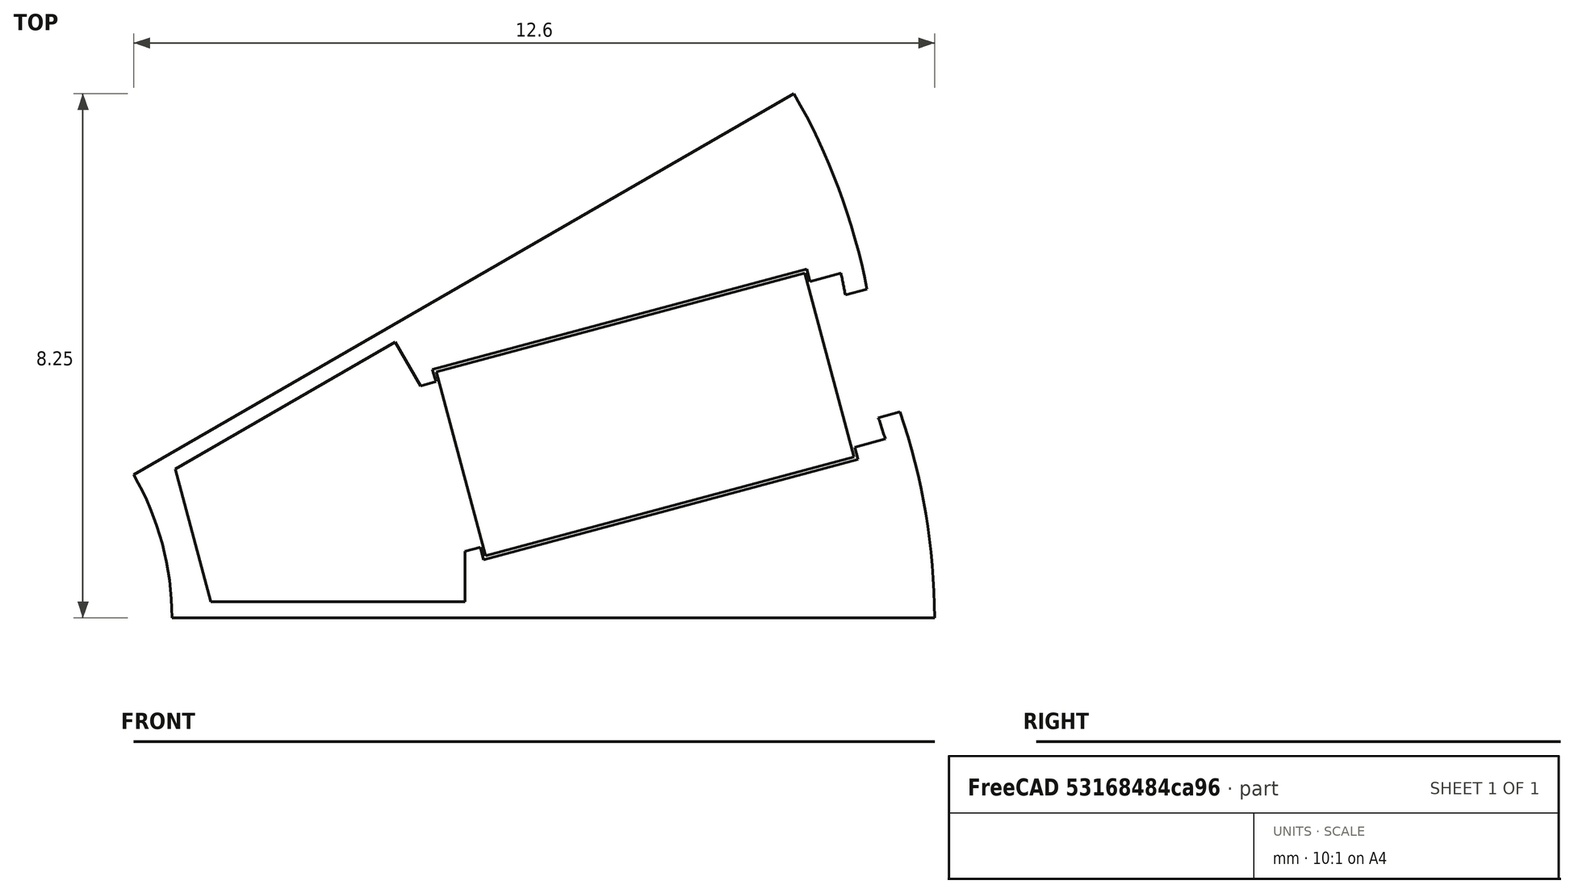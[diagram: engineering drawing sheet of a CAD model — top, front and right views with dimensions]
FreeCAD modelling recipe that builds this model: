
FCSTD DOCUMENT  (FreeCAD 0.18R4 (GitTag))
Label: rotor2
License: All rights reserved
LicenseURL: http://en.wikipedia.org/wiki/All_rights_reserved
objects: Sketcher::SketchObject×6, Surface::Filling×3, PartDesign::Body×2, Spreadsheet::Sheet×1, Part::Cut×1
note: 12 computed .brp shape members not serialized (recipe doc carries the construction recipe); baked Part::Feature solids carry a one-line shape summary decoded from their .brp

FEATURE [Spreadsheet::Sheet] Spreadsheet  label="Variables"
  cells = A1=poleNumber; B1(poleNumber)=12; A2=outerDiameter; B2(outerDiameter)=33; A3=innerDiameter; B3(innerDiameter)=9; D3=Calc Value; A4=stackLength; B4(stackLength)=20; D4=Input Value; A5=stackingFactor; B5(stackingFactor)=0.95; A6=embrace; B6(embrace)=75; A7=contourRatio; B7(contourRatio)=60; A8=magnetAirgap; B8(magnetAirgap)=0.05; A9=poleSeparation; B9(poleSeparation)=2; A10=magnetWidth; B10(magnetWidth)=3; A11=magnetHeight; B11(magnetHeight)=6; A12=rib; B12(rib)=0.5; A13=bridgeCurved; B13(bridgeCurved)=0.35; A14=cutTop; B14(cutTop)=0.2; A15=cutBottom; B15(cutBottom)=0.25; A16=segmentAngle; B16(segmentAngle)==360 / poleNumber; A17=movePocketInwards; B17(movePocketInwards)=0.5; A18=cuttingThickness; B18(cuttingThickness)=0.1; A19=magnetLength; B19(magnetLength)==stackLength; A20=cut; B20(cut)=0.2; A21=ribShaft; B21(ribShaft)=0.5; A22=magnetEmbrace; B22(magnetEmbrace)=70; A23=magnetContourRatio; B23(magnetContourRatio)=95; A24=axialMisalignment; B24(axialMisalignment)=0.5
FEATURE [Sketcher::SketchObject] Sketch003  label="RotorPoleSketch"
  MapMode = 5
  Support = -> [XY_Plane]
  expr: Constraints[21] = Variables.innerDiameter / 2
  expr: Constraints[27] = Variables.segmentAngle / 2
  expr: Constraints[9] = Variables.outerDiameter / 2 * Variables.contourRatio / 100
  expr: Constraints[14] = Variables.poleSeparation
  expr: Constraints[11] = Variables.outerDiameter / 2 * Variables.contourRatio / 100
  expr: Constraints[6] = Variables.outerDiameter / 2
  expr: Constraints[5] = Variables.segmentAngle
  sketch-geometry (10):
    g0: LineSegment [constr] StartX=0 StartY=-1e-16 StartZ=0 EndX=16.5 EndY=-1e-16 EndZ=0
    g1: LineSegment [constr] StartX=0 StartY=-1e-16 StartZ=0 EndX=14.2894 EndY=8.25 EndZ=0
    g2: ArcOfCircle [constr] CenterX=0 CenterY=-1e-16 CenterZ=0 NormalX=0 NormalY=0 NormalZ=1 AngleXU=0 Radius=16.5 StartAngle=0 EndAngle=0.523599
    g3: ArcOfCircle CenterX=5.71577 CenterY=3.3 CenterZ=0 NormalX=0 NormalY=0 NormalZ=1 AngleXU=0 Radius=9.9 StartAngle=0.190202 EndAngle=0.523599
    g4: ArcOfCircle CenterX=6.6 CenterY=-5.416e-11 CenterZ=0 NormalX=0 NormalY=0 NormalZ=1 AngleXU=0 Radius=9.9 StartAngle=5.4707e-12 EndAngle=0.333396
    g5: LineSegment StartX=15.4372 StartY=5.17167 StartZ=0 EndX=15.9549 EndY=3.23982 EndZ=0
    g6: LineSegment [constr] StartX=0 StartY=0 StartZ=0 EndX=15.9378 EndY=4.27051 EndZ=0
    g7: ArcOfCircle CenterX=0 CenterY=0 CenterZ=0 NormalX=0 NormalY=0 NormalZ=1 AngleXU=0 Radius=4.5 StartAngle=0 EndAngle=0.523599
    g8: LineSegment StartX=3.89711 StartY=2.25 StartZ=0 EndX=14.2894 EndY=8.25 EndZ=0
    g9: LineSegment StartX=4.5 StartY=0 StartZ=0 EndX=16.5 EndY=-1e-16 EndZ=0
  constraints (28):
    c: Coincident(g0,g-1)
    c: Coincident(g1,g0)
    c: Coincident(g2,g0)
    c: Coincident(g2,g0)
    c: Coincident(g2,g1)
    c: Angle(g0,g1) = 0.523599
    c: Radius(g2) = 16.5
    c: PointOnObject(g3,g1)
    c: Coincident(g3,g1)
    c: Radius(g3) = 9.9
    c: Coincident(g4,g0)
    c: Radius(g4) = 9.9
    c: Coincident(g5,g3)
    c: Coincident(g5,g4)
    c: Distance(g5) = 2
    c: Coincident(g6,g-1)
    c: PointOnObject(g6,g2)
    c: Symmetric(g3,g4,g6)
    c: Coincident(g7,g-1)
    c: PointOnObject(g7,g1)
    c: PointOnObject(g7,g0)
    c: Radius(g7) = 4.5
    c: Coincident(g8,g7)
    c: Coincident(g8,g3)
    c: Coincident(g9,g7)
    c: Coincident(g9,g4)
    c: Horizontal(g0)
    c: Angle(g-1,g6) = 0.261799
FEATURE [Sketcher::SketchObject] Sketch004  label="BoundingBox"
  MapMode = 5
  Support = -> [XY_Plane]
  expr: Constraints[8] = Variables.outerDiameter
  sketch-geometry (6):
    g0: LineSegment StartX=-16.5 StartY=-16.5 StartZ=0 EndX=16.5 EndY=-16.5 EndZ=0
    g1: LineSegment StartX=16.5 StartY=-16.5 StartZ=0 EndX=16.5 EndY=16.5 EndZ=0
    g2: LineSegment StartX=16.5 StartY=16.5 StartZ=0 EndX=-16.5 EndY=16.5 EndZ=0
    g3: LineSegment StartX=-16.5 StartY=16.5 StartZ=0 EndX=-16.5 EndY=-16.5 EndZ=0
    g4: LineSegment [constr] StartX=-16.5 StartY=-16.5 StartZ=0 EndX=16.5 EndY=16.5 EndZ=0
    g5: GeomPoint X=0 Y=0 Z=0
  constraints (14):
    c: Coincident(g0,g1)
    c: Coincident(g1,g2)
    c: Coincident(g2,g3)
    c: Coincident(g3,g0)
    c: Horizontal(g0)
    c: Horizontal(g2)
    c: Vertical(g1)
    c: Vertical(g3)
    c: DistanceY(g1,g1) = 33
    c: Equal(g2,g1)
    c: Coincident(g4,g0)
    c: Coincident(g4,g1)
    c: Symmetric(g0,g1,g5)
    c: Coincident(g-1,g5)
FEATURE [Sketcher::SketchObject] Sketch005  label="RotorSideSketch"
  MapMode = 5
  Support = -> [XY_Plane001]
  expr: Constraints[22] = Variables.stackLength / 2 - Variables.axialMisalignment
  expr: Constraints[9] = Variables.outerDiameter / 2
  expr: Constraints[8] = Variables.innerDiameter / 2
  expr: Constraints[7] = Variables.stackLength
  sketch-geometry (8):
    g0: LineSegment StartX=-9.5 StartY=4.5 StartZ=0 EndX=10.5 EndY=4.5 EndZ=0
    g1: LineSegment StartX=10.5 StartY=4.5 StartZ=0 EndX=10.5 EndY=16.5 EndZ=0
    g2: LineSegment StartX=10.5 StartY=16.5 StartZ=0 EndX=-9.5 EndY=16.5 EndZ=0
    g3: LineSegment StartX=-9.5 StartY=16.5 StartZ=0 EndX=-9.5 EndY=4.5 EndZ=0
    g4: LineSegment StartX=-9.5 StartY=-4.5 StartZ=0 EndX=10.5 EndY=-4.5 EndZ=0
    g5: LineSegment StartX=10.5 StartY=-4.5 StartZ=0 EndX=10.5 EndY=-16.5 EndZ=0
    g6: LineSegment StartX=10.5 StartY=-16.5 StartZ=0 EndX=-9.5 EndY=-16.5 EndZ=0
    g7: LineSegment StartX=-9.5 StartY=-16.5 StartZ=0 EndX=-9.5 EndY=-4.5 EndZ=0
  constraints (23):
    c: Coincident(g0,g1)
    c: Coincident(g1,g2)
    c: Coincident(g2,g3)
    c: Coincident(g3,g0)
    c: Horizontal(g0)
    c: Vertical(g1)
    c: Vertical(g3)
    c: DistanceX(g2,g2) = 20
    c: DistanceY(g-1,g0) = 4.5
    c: DistanceY(g-1,g1) = 16.5
    c: Coincident(g4,g5)
    c: Coincident(g5,g6)
    c: Coincident(g6,g7)
    c: Coincident(g7,g4)
    c: Horizontal(g4)
    c: Vertical(g5)
    c: Vertical(g7)
    c: Equal(g4,g0)
    c: Equal(g7,g3)
    c: Horizontal(g2)
    c: Horizontal(g6)
    c: Symmetric(g4,g0,g-1)
    c: DistanceX(g0,g-1) = 9.5
FEATURE [Sketcher::SketchObject] Sketch006  label="MagnetSideSketch"
  ExternalGeometry = -> [Sketch005]
  MapMode = 5
  Support = -> [XY_Plane001]
  expr: Constraints[23] = Variables.stackLength / 2 - Variables.axialMisalignment
  expr: Constraints[12] = Variables.bridgeCurved + Variables.movePocketInwards
  expr: Constraints[8] = Variables.magnetHeight
  expr: Constraints[7] = Variables.magnetLength
  sketch-geometry (9):
    g0: LineSegment StartX=-9.5 StartY=9.65 StartZ=0 EndX=10.5 EndY=9.65 EndZ=0
    g1: LineSegment StartX=10.5 StartY=9.65 StartZ=0 EndX=10.5 EndY=15.65 EndZ=0
    g2: LineSegment StartX=10.5 StartY=15.65 StartZ=0 EndX=-9.5 EndY=15.65 EndZ=0
    g3: LineSegment StartX=-9.5 StartY=15.65 StartZ=0 EndX=-9.5 EndY=9.65 EndZ=0
    g4: LineSegment [constr] StartX=10.5 StartY=15.65 StartZ=0 EndX=10.5 EndY=16.5 EndZ=0
    g5: LineSegment StartX=-9.5 StartY=-15.65 StartZ=0 EndX=10.5 EndY=-15.65 EndZ=0
    g6: LineSegment StartX=10.5 StartY=-15.65 StartZ=0 EndX=10.5 EndY=-9.65 EndZ=0
    g7: LineSegment StartX=10.5 StartY=-9.65 StartZ=0 EndX=-9.5 EndY=-9.65 EndZ=0
    g8: LineSegment StartX=-9.5 StartY=-9.65 StartZ=0 EndX=-9.5 EndY=-15.65 EndZ=0
  constraints (25):
    c: Coincident(g0,g1)
    c: Coincident(g1,g2)
    c: Coincident(g2,g3)
    c: Coincident(g3,g0)
    c: Horizontal(g0)
    c: Vertical(g1)
    c: Vertical(g3)
    c: DistanceX(g2,g2) = 20
    c: DistanceY(g1,g1) = 6
    c: Coincident(g4,g1)
    c: PointOnObject(g4,g-3)
    c: Angle(g4,g2) = 1.5708
    c: DistanceY(g4,g4) = 0.85
    c: Coincident(g5,g6)
    c: Coincident(g6,g7)
    c: Coincident(g7,g8)
    c: Coincident(g8,g5)
    c: Horizontal(g5)
    c: Vertical(g6)
    c: Vertical(g8)
    c: Symmetric(g7,g0,g-1)
    c: Symmetric(g6,g0,g-1)
    c: Equal(g8,g3)
    c: DistanceX(g0,g-1) = 9.5
    c: Horizontal(g2)
FEATURE [PartDesign::Body] Body001  label="SideView"
  Group = -> [Sketch005,Sketch006]
  Origin = -> Origin001
FEATURE [Surface::Filling] Surface001  label="RotorPoleSketch_Surface"
  Anisotropy = false
  BoundaryEdges = -> [Sketch003]
  BoundaryOrder = [0,0,0,0,0,0]
  Degree = 3
  Iterations = 2
  MaximumDegree = 8
  MaximumSegments = 9
  PointsOnCurve = 15
  TolAngular = 0.01
  TolCurvature = 0.1
  Tolerance2d = 1e-05
  Tolerance3d = 0.0001
FEATURE [Sketcher::SketchObject] Sketch008  label="PocketSketch"
  MapMode = 5
  Support = -> [XY_Plane]
  expr: Constraints[89] = Variables.innerDiameter / 2 + Variables.ribShaft
  expr: Constraints[48] = Variables.magnetWidth + 2 * Variables.magnetAirgap
  expr: Constraints[36] = Variables.magnetWidth + 2 * Variables.magnetAirgap - 2 * Variables.cut
  expr: Constraints[66] = Variables.rib / 2
  expr: Constraints[25] = Variables.outerDiameter / 2 * Variables.contourRatio / 100 - Variables.bridgeCurved
  expr: Constraints[21] = Variables.segmentAngle / 2
  expr: Constraints[55] = Variables.magnetHeight + 2 * Variables.magnetAirgap
  expr: Constraints[41] = Variables.movePocketInwards
  expr: Constraints[9] = Variables.outerDiameter / 2 * Variables.contourRatio / 100
  expr: Constraints[14] = Variables.poleSeparation
  expr: Constraints[23] = Variables.outerDiameter / 2 * Variables.contourRatio / 100 - Variables.bridgeCurved
  expr: Constraints[19] = Variables.innerDiameter / 2
  expr: Constraints[11] = Variables.outerDiameter / 2 * Variables.contourRatio / 100
  expr: Constraints[6] = Variables.outerDiameter / 2
  expr: Constraints[72] = Variables.rib / 2
  expr: Constraints[5] = Variables.segmentAngle
  sketch-geometry (31):
    g0: LineSegment [constr] StartX=0 StartY=-5e-16 StartZ=0 EndX=16.5 EndY=-5e-16 EndZ=0
    g1: LineSegment [constr] StartX=0 StartY=-5e-16 StartZ=0 EndX=14.2894 EndY=8.25 EndZ=0
    g2: ArcOfCircle [constr] CenterX=0 CenterY=-5e-16 CenterZ=0 NormalX=0 NormalY=0 NormalZ=1 AngleXU=0 Radius=16.5 StartAngle=0 EndAngle=0.523599
    g3: ArcOfCircle [constr] CenterX=5.71577 CenterY=3.3 CenterZ=0 NormalX=0 NormalY=0 NormalZ=1 AngleXU=0 Radius=9.9 StartAngle=0.190202 EndAngle=0.523599
    g4: ArcOfCircle [constr] CenterX=6.6 CenterY=-3.5e-15 CenterZ=0 NormalX=0 NormalY=0 NormalZ=1 AngleXU=0 Radius=9.9 StartAngle=3e-16 EndAngle=0.333396
    g5: LineSegment StartX=15.4372 StartY=5.17167 StartZ=0 EndX=15.9549 EndY=3.23982 EndZ=0
    g6: LineSegment [constr] StartX=0 StartY=0 StartZ=0 EndX=15.6961 EndY=4.20574 EndZ=0
    g7: ArcOfCircle [constr] CenterX=0 CenterY=0 CenterZ=0 NormalX=0 NormalY=0 NormalZ=1 AngleXU=0 Radius=4.5 StartAngle=0 EndAngle=0.523599
    g8: ArcOfCircle CenterX=5.71577 CenterY=3.3 CenterZ=0 NormalX=0 NormalY=0 NormalZ=1 AngleXU=0 Radius=9.55 StartAngle=0.187574 EndAngle=0.224282
    g9: ArcOfCircle CenterX=6.6 CenterY=-3.5e-15 CenterZ=0 NormalX=0 NormalY=0 NormalZ=1 AngleXU=0 Radius=9.55 StartAngle=0.299317 EndAngle=0.336025
    g10: LineSegment StartX=15.0983 StartY=5.08084 StartZ=0 EndX=15.4372 EndY=5.17167 EndZ=0
    g11: LineSegment StartX=15.6159 StartY=3.14899 StartZ=0 EndX=15.9549 EndY=3.23982 EndZ=0
    g12: LineSegment [constr] StartX=15.0266 StartY=5.42398 StartZ=0 EndX=15.7254 EndY=2.81598 EndZ=0
    g13: LineSegment StartX=15.0266 StartY=5.42398 StartZ=0 EndX=14.5436 EndY=5.29457 EndZ=0
    g14: LineSegment StartX=15.7254 StartY=2.81598 StartZ=0 EndX=15.2424 EndY=2.68657 EndZ=0
    g15: LineSegment StartX=14.5436 StartY=5.29457 StartZ=0 EndX=14.4919 EndY=5.48776 EndZ=0
    g16: LineSegment StartX=15.2424 StartY=2.68657 StartZ=0 EndX=15.2942 EndY=2.49339 EndZ=0
    g17: LineSegment StartX=14.4919 StartY=5.48776 StartZ=0 EndX=8.5997 EndY=3.90896 EndZ=0
    g18: LineSegment StartX=15.2942 StartY=2.49339 StartZ=0 EndX=9.40204 EndY=0.914592 EndZ=0
    g19: LineSegment StartX=8.5997 StartY=3.90896 StartZ=0 EndX=8.65147 EndY=3.71578 EndZ=0
    g20: LineSegment StartX=9.40204 StartY=0.914592 StartZ=0 EndX=9.35028 EndY=1.10778 EndZ=0
    g21: LineSegment StartX=8.65147 StartY=3.71578 StartZ=0 EndX=8.40999 EndY=3.65107 EndZ=0
    g22: LineSegment StartX=9.35028 StartY=1.10778 StartZ=0 EndX=9.1088 EndY=1.04307 EndZ=0
    g23: LineSegment StartX=8.40999 StartY=3.65107 StartZ=0 EndX=8.01345 EndY=4.33789 EndZ=0
    g24: LineSegment [constr] StartX=8.01345 StartY=4.33789 StartZ=0 EndX=7.88845 EndY=4.5544 EndZ=0
    g25: LineSegment StartX=9.1088 StartY=1.04307 StartZ=0 EndX=9.1088 EndY=0.25 EndZ=0
    g26: LineSegment [constr] StartX=9.1088 StartY=0.25 StartZ=0 EndX=9.1088 EndY=0 EndZ=0
    g27: LineSegment StartX=8.01345 StartY=4.33789 StartZ=0 EndX=4.54986 EndY=2.33819 EndZ=0
    g28: LineSegment StartX=4.54986 StartY=2.33819 StartZ=0 EndX=5.10939 EndY=0.25 EndZ=0
    g29: LineSegment StartX=5.10939 StartY=0.25 StartZ=0 EndX=9.1088 EndY=0.25 EndZ=0
    g30: LineSegment [constr] StartX=0 StartY=0 StartZ=0 EndX=4.82963 EndY=1.2941 EndZ=0
  constraints (91):
    c: Coincident(g0,g-1)
    c: Coincident(g1,g0)
    c: Coincident(g2,g0)
    c: Coincident(g2,g0)
    c: Coincident(g2,g1)
    c: Angle(g0,g1) = 0.523599
    c: Radius(g2) = 16.5
    c: PointOnObject(g3,g1)
    c: Coincident(g3,g1)
    c: Radius(g3) = 9.9
    c: Coincident(g4,g0)
    c: Radius(g4) = 9.9
    c: Coincident(g5,g3)
    c: Coincident(g5,g4)
    c: Distance(g5) = 2
    c: Coincident(g6,g-1)
    c: Coincident(g7,g-1)
    c: PointOnObject(g7,g1)
    c: PointOnObject(g7,g0)
    c: Radius(g7) = 4.5
    c: Horizontal(g0)
    c: Angle(g-1,g6) = 0.261799
    c: Coincident(g8,g3)
    c: Radius(g8) = 9.55
    c: Coincident(g9,g4)
    c: Radius(g9) = 9.55
    c: Coincident(g10,g8)
    c: Coincident(g10,g3)
    c: Coincident(g11,g9)
    c: Coincident(g11,g4)
    c: Parallel(g11,g6)
    c: Parallel(g10,g6)
    c: Symmetric(g11,g10,g6)
    c: PointOnObject(g6,g5)
    c: Coincident(g12,g8)
    c: Coincident(g12,g9)
    c: Distance(g12) = 2.7
    c: Perpendicular(g6,g12)
    c: Coincident(g13,g8)
    c: Coincident(g14,g9)
    c: Equal(g14,g13)
    c: Distance(g13) = 0.5
    c: Angle(g13,g12) = 1.5708
    c: Angle(g12,g14) = 1.5708
    c: Coincident(g15,g13)
    c: Coincident(g16,g14)
    c: Angle(g13,g15) = 1.5708
    c: Angle(g16,g14) = 1.5708
    c: Distance(g15,g16) = 3.1
    c: Equal(g15,g16)
    c: Coincident(g17,g15)
    c: Coincident(g18,g16)
    c: Equal(g17,g18)
    c: Parallel(g17,g6)
    c: Parallel(g18,g6)
    c: Distance(g17) = 6.1
    c: Coincident(g19,g17)
    c: Coincident(g20,g18)
    c: Equal(g19,g20)
    c: Equal(g19,g15)
    c: Angle(g18,g20) = 1.5708
    c: Angle(g19,g17) = 1.5708
    c: Coincident(g21,g19)
    c: Coincident(g22,g20)
    c: Parallel(g22,g21)
    c: Equal(g21,g22)
    c: Distance(g21) = 0.25
    c: Angle(g19,g21) = 1.5708
    c: Coincident(g23,g21)
    c: Coincident(g24,g23)
    c: PointOnObject(g24,g1)
    c: Parallel(g24,g23)
    c: Distance(g24) = 0.25
    c: Angle(g1,g24) = 1.5708
    c: Coincident(g25,g22)
    c: Coincident(g26,g25)
    c: PointOnObject(g26,g0)
    c: Parallel(g26,g25)
    c: Equal(g26,g24)
    c: Vertical(g26)
    c: Coincident(g27,g23)
    c: Coincident(g28,g27)
    c: Coincident(g29,g28)
    c: Coincident(g29,g25)
    c: Horizontal(g29)
    c: Parallel(g27,g1)
    c: Equal(g27,g29)
    c: Coincident(g30,g-1)
    c: PointOnObject(g30,g28)
    c: Distance(g30) = 5
    c: Angle(g30,g28) = 1.5708
FEATURE [Surface::Filling] Surface  label="PocketSketch_Surface"
  Anisotropy = false
  BoundaryEdges = -> [Sketch008]
  BoundaryOrder = [0,0,0,0,0,0,0,0,0,0,0,0,0,0,0,0,0,0,0,0]
  Degree = 3
  Iterations = 2
  MaximumDegree = 8
  MaximumSegments = 9
  PointsOnCurve = 15
  TolAngular = 0.01
  TolCurvature = 0.1
  Tolerance2d = 1e-05
  Tolerance3d = 0.0001
FEATURE [Part::Cut] Cut  label="Rotor_Surface"
  Base = -> Surface001
  Tool = -> Surface
FEATURE [Sketcher::SketchObject] Sketch  label="MagnetSketch"
  ExternalGeometry = -> [Sketch008]
  MapMode = 5
  Support = -> [XY_Plane]
  expr: Constraints[9] = Variables.magnetHeight
  expr: Constraints[16] = Variables.magnetAirgap
  expr: Constraints[8] = Variables.magnetWidth
  sketch-geometry (6):
    g0: LineSegment StartX=9.4374 StartY=0.975829 StartZ=0 EndX=15.233 EndY=2.52874 EndZ=0
    g1: LineSegment StartX=15.233 StartY=2.52874 StartZ=0 EndX=14.4565 EndY=5.42652 EndZ=0
    g2: LineSegment StartX=14.4565 StartY=5.42652 StartZ=0 EndX=8.66094 EndY=3.87361 EndZ=0
    g3: LineSegment StartX=8.66094 StartY=3.87361 StartZ=0 EndX=9.4374 EndY=0.975829 EndZ=0
    g4: LineSegment [constr] StartX=14.4565 StartY=5.42652 StartZ=0 EndX=14.4436 EndY=5.47482 EndZ=0
    g5: LineSegment [constr] StartX=14.4565 StartY=5.42652 StartZ=0 EndX=14.5048 EndY=5.43946 EndZ=0
  constraints (18):
    c: Coincident(g0,g1)
    c: Coincident(g1,g2)
    c: Coincident(g2,g3)
    c: Coincident(g3,g0)
    c: Parallel(g2,g-4)
    c: Parallel(g1,g-3)
    c: Parallel(g2,g0)
    c: Parallel(g3,g1)
    c: Distance(g1) = 3
    c: Distance(g2) = 6
    c: Coincident(g4,g1)
    c: PointOnObject(g4,g-4)
    c: Coincident(g5,g1)
    c: PointOnObject(g5,g-3)
    c: Angle(g5,g4) = 1.5708
    c: Equal(g5,g4)
    c: Distance(g4) = 0.05
    c: Angle(g1,g5) = 1.5708
FEATURE [PartDesign::Body] Body  label="TopView"
  Group = -> [Sketch003,Sketch004,Sketch008,Sketch]
  Origin = -> Origin
FEATURE [Surface::Filling] Surface002  label="Magnet_Surface"
  Anisotropy = false
  BoundaryEdges = -> [Sketch]
  BoundaryOrder = [0,0,0,0]
  Degree = 3
  Iterations = 2
  MaximumDegree = 8
  MaximumSegments = 9
  PointsOnCurve = 15
  TolAngular = 0.01
  TolCurvature = 0.1
  Tolerance2d = 1e-05
  Tolerance3d = 0.0001
